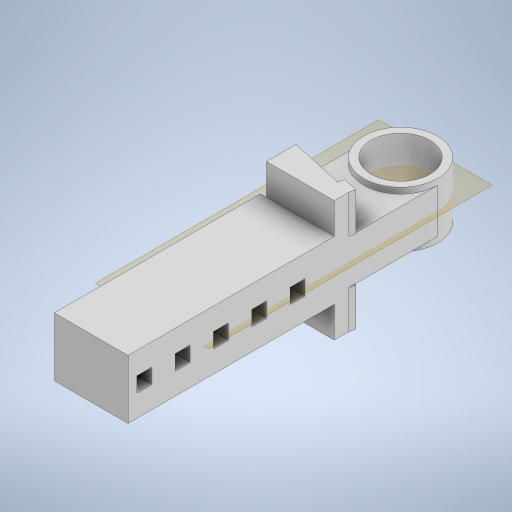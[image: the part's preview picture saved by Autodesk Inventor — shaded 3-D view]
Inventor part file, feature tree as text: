
AUTODESK INVENTOR PART (.ipt)
format: ipt  version: 2023 (Build 270158000, 158)  size: 369,152 bytes
history: native  units: mm
features: sketch x13, extrude x10, plane x1, mirror x1
ambient origin geometry x8: Origin, YZ Plane, XZ Plane, XY Plane, X Axis, Y Axis, Z Axis, Center Point
bodies: Solid1 (feature_tree)
feature tree (25):
  extrude  "Extrusion1"  Depth=25.0mm
  sketch  "Sketch3"  dims[d2=50.0mm d3=15.0mm d4=0.0mm]
  extrude  "Extrusion3"  Depth=15.0mm TaperAngle=0.0deg
  extrude  "Extrusion7"  Depth=30.0mm
  sketch  "Sketch10"  dims[d65=7.5mm d66=5.0mm]
  plane  "Work Plane1"
  mirror  "Mirror1"
  extrude  "Extrusion9"  Depth=13.0mm TaperAngle=0.0deg
  extrude  "Extrusion10"  Depth=5.0mm
  extrude  "Extrusion11"  Depth=25.0mm
  sketch  "Sketch18"  dims[d77=2.5mm d78=0.0mm d79=30.0mm d80=0.0mm]
  extrude  "Extrusion12"  Depth=2.0mm TaperAngle=0.0deg
  extrude  "Extrusion13"  Depth=2.5mm TaperAngle=0.0deg
  extrude  "Extrusion14"  Depth=30.0mm TaperAngle=0.0deg
  extrude  "Extrusion15"  Depth=5.0mm
  sketch  "Sketch1"  dims[d0=20.0mm d1=25.0mm]
  sketch  "Sketch4"  dims[d13=25.0mm d14=0.0mm d50=30.0mm]
  sketch  "Sketch9"  dims[d51=2.0mm d52=13.0mm d53=0.0mm]
  sketch  "Sketch15"  dims[d67=2.0mm d68=0.0mm d69=25.0mm]
  sketch  "Sketch16"  dims[d70=2.0mm d71=0.0mm d72=2.0mm d73=0.0mm]
  sketch  "Sketch17"  dims[d74=10.0mm d75=2.5mm d76=0.0mm]
  sketch  "Sketch19"  dims[d81=10.0mm d82=5.0mm]
  sketch  "Sketch20"  dims[d83=5.0mm]
  sketch  "Sketch21"  dims[d84=8.0mm]
  sketch  "Sketch22"  dims[d85=5.0mm d86=8.0mm d87=8.0mm d88=8.0mm d89=30.0mm d90=0.0mm d36=0.5mm d37=0.872665mm d38=0.5mm d39=0.872665mm]
